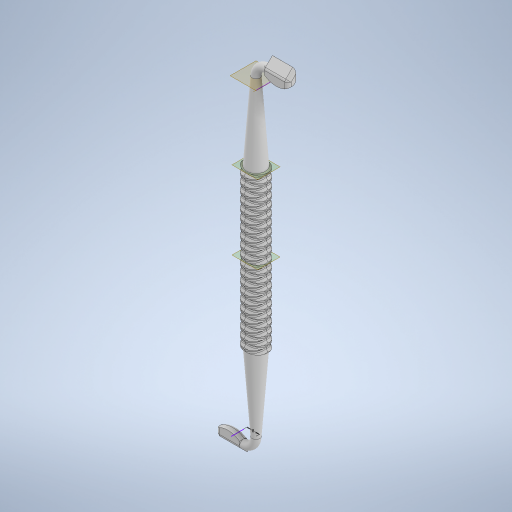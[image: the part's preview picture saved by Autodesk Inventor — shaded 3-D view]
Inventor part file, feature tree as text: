
AUTODESK INVENTOR PART (.ipt)
format: ipt  version: 2024 (Build 280153000, 153)  size: 2,723,840 bytes
history: native  units: mm
features: sketch x15, chamfer x12, extrude x7, helix x4, plane x3, fillet x3, revolve x2, other x1
ambient origin geometry x8: Origin, YZ Plane, XZ Plane, XY Plane, X Axis, Y Axis, Z Axis, Center Point
bodies: Solid1 (feature_tree)
feature tree (47):
  extrude  "Extrusion1"  Depth=2.0mm TaperAngle=0.0deg
  helix  "Coil1"  [1 undecoded]
  helix  "Coil2"  [1 undecoded]
  helix  "Coil3"  [1 undecoded]
  helix  "Coil4"  [1 undecoded]
  chamfer  "Chamfer1"  Distance=2.0mm Angle=45.0deg
  chamfer  "Chamfer2"  Distance=2.0mm Angle=45.0deg
  chamfer  "Chamfer3"  Distance=2.0mm Angle=45.0deg
  chamfer  "Chamfer4"  Distance=2.0mm Angle=45.0deg
  chamfer  "Chamfer5"  Distance=2.0mm Angle=45.0deg
  chamfer  "Chamfer6"  Distance=2.0mm Angle=45.0deg
  chamfer  "Chamfer7"  Distance=2.0mm Angle=45.0deg
  chamfer  "Chamfer8"  Distance=50.0mm
  extrude  "Extrusion2"  TaperAngle=90.0deg  [1 undecoded]
  chamfer  "Chamfer9"  Distance=50.0mm
  sketch  "Sketch9"  dims[d65=50.0mm d66=50.0mm d67=0.698132mm d68=90.0deg]
  plane  "Work Plane3"
  sketch  "Sketch10"  dims[d69=-50.0mm]
  other  "Work Axis2"
  revolve  "Revolution1"  [1 undecoded]
  plane  "Work Plane4"
  plane  "Work Plane5"
  extrude  "Extrusion3"  Depth=15.0mm TaperAngle=0.0deg
  chamfer  "Chamfer10"  Distance=15.0mm
  sketch  "Sketch12"  dims[d71=12.0mm d72=50.0mm d73=0.0mm]
  revolve  "Revolution2"  [1 undecoded]
  extrude  "Extrusion4"  Depth=15.0mm TaperAngle=0.0deg
  extrude  "Extrusion5"  Depth=13.0mm
  chamfer  "Chamfer11"  Distance=15.0mm
  fillet  "Fillet1"  Radius=2.0mm
  extrude  "Extrusion6"  Depth=2.0mm
  extrude  "Extrusion7"  Depth=2.0mm
  chamfer  "Chamfer12"  [1 undecoded]
  fillet  "Fillet2"  [1 undecoded]
  fillet  "Fillet3"  [1 undecoded]
  sketch  "Sketch1"  dims[d0=15.0mm d1=100.0mm d2=0.0mm d3=2.0mm]
  sketch  "Sketch2"  dims[d4=10.0mm d5=10.0mm d6=100.0mm d7=0.0mm d8=90.0deg d9=90.0deg d10=0.0mm d11=0.0mm]
  sketch  "Sketch4"  dims[d12=10.0mm d13=10.0mm d14=100.0mm d15=0.0mm d16=90.0deg d17=90.0deg d18=0.0mm d19=0.0mm d20=2.0mm]
  sketch  "Sketch5"  dims[d21=10.0mm d22=10.0mm d23=100.0mm d24=0.0mm d25=90.0deg d26=90.0deg d27=0.0mm d28=0.0mm d29=2.0mm]
  sketch  "Sketch6"  dims[d30=10.0mm d31=10.0mm d32=100.0mm d33=0.0mm d34=90.0deg d35=90.0deg d36=0.0mm d37=0.0mm d38=1.0mm d39=2.0mm d40=45.0deg d41=1.0mm d42=2.0mm d43=45.0deg d44=1.0mm d45=2.0mm d46=45.0deg d47=1.0mm d48=2.0mm d49=45.0deg d50=1.0mm d51=2.0mm d52=45.0deg d53=1.0mm d54=2.0mm d55=45.0deg d56=1.0mm d57=2.0mm d58=45.0deg d59=1.0mm d60=2.0mm d61=45.0deg]
  sketch  "Sketch8"  dims[d62=12.0mm d63=50.0mm d64=0.0mm]
  sketch  "Sketch11"  dims[d70=-100.0mm]
  sketch  "Sketch13"  dims[d74=50.0mm d75=50.0mm d76=0.698132mm d77=8.0mm]
  sketch  "Sketch14"  dims[d78=90.0deg d79=15.0mm d80=0.0mm]
  sketch  "Sketch15"  dims[d81=13.0mm d82=15.0mm d83=0.0mm]
  sketch  "Sketch16"  dims[d84=5.0mm d85=2.0mm d86=45.0deg d87=2.0mm]
  sketch  "Sketch17"  dims[d88=5.007mm d89=15.0mm d90=0.0mm d91=13.0mm d92=15.0mm d93=0.0mm d94=5.0mm d95=2.0mm d96=45.0deg d97=2.0mm d98=2.0mm]
note: 10 required parameter values undecoded (feature->parameter linkage not recoverable at this tier; creation-order binding heuristic only, values carry confidence <= 0.55)